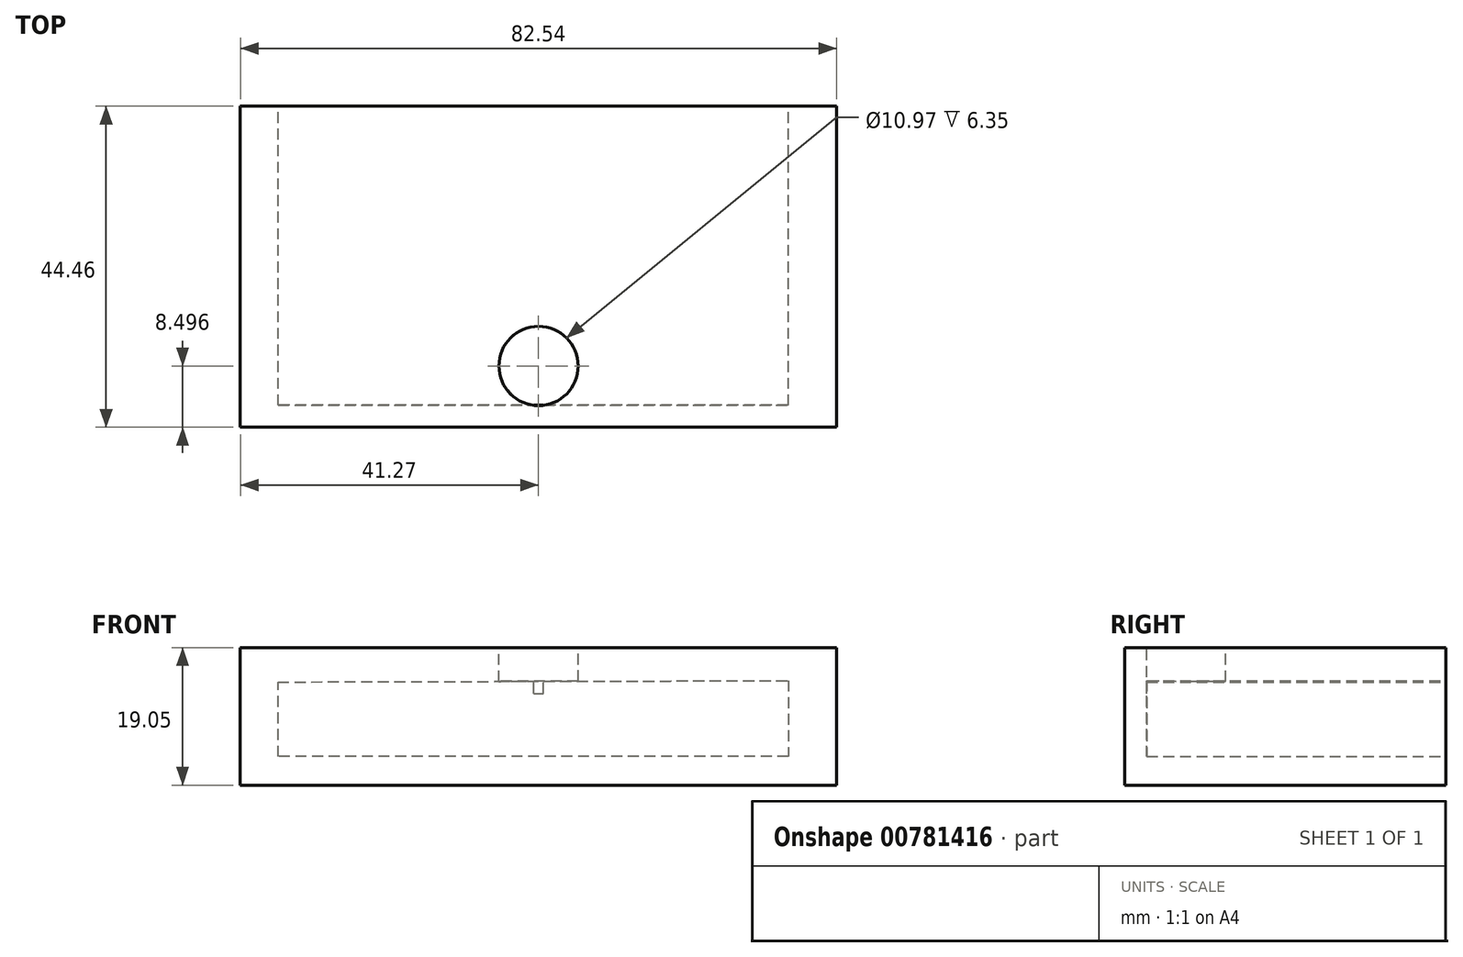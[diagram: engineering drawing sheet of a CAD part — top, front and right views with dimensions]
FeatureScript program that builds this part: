
annotation { "Feature Type Name" : "Feature", "Feature Type Description" : "" }
export const myFeature = defineFeature(function(context is Context, id is Id, definition is map)
    precondition{}
    {
        {
            var Q0;
            Q0=qCreatedBy(makeId("Top.planeOp"),FACE);
            var sketch = newSketch(context, id + "F0", { "sketchPlane" : qUnion([Q0])});
            skLineSegment(sketch, "E0.bottom", {"start": v(41.28, -22.22) * mm, "end": v(-41.28, -22.23) * mm});
            skLineSegment(sketch, "E0.top", {"start": v(41.28, 22.23) * mm, "end": v(-41.28, 22.23) * mm});
            skLineSegment(sketch, "E0.left", {"start": v(41.28, -22.22) * mm, "end": v(41.28, 22.23) * mm});
            skLineSegment(sketch, "E0.right", {"start": v(-41.28, -22.23) * mm, "end": v(-41.28, 22.23) * mm});
            skPoint(sketch, "E0.middle", {"position": v(0, 0) * mm});
            skSolve(sketch);
        }
        {
            var Q0;
            Q0 = qSketchRegion(id + "F0", true);
            extrude(context, id + "F1", {"entities" : qUnion([Q0]), "depth" : 19.05 * mm, "offsetDistance" : 25.4 * mm});
        }
        {
            var Q0;
            Q0=makeQuery(id+"F1.opExtrude","SWEPT_FACE",FACE,{"disambiguationData":[OSD([sQuery(id+"F0.wireOp",EDGE,"E0.top")])]});
            var sketch = newSketch(context, id + "F2", { "sketchPlane" : qUnion([Q0])});
            skLineSegment(sketch, "E1", {"start": v(-34.57, 14.47) * mm, "end": v(-34.57, 3.96) * mm});
            skLineSegment(sketch, "E2", {"start": v(-34.57, 3.96) * mm, "end": v(36.04, 3.96) * mm});
            skLineSegment(sketch, "E3", {"start": v(36.04, 3.96) * mm, "end": v(36.04, 14.29) * mm});
            skLineSegment(sketch, "E4", {"start": v(36.04, 14.29) * mm, "end": v(-34.57, 14.47) * mm});
            skSolve(sketch);
        }
        {
            var Q0;
            Q0 = qSketchRegion(id + "F2", true);
            extrude(context, id + "F3", {"entities" : qUnion([Q0]), "operationType" : NewBodyOperationType.REMOVE, "oppositeDirection" : true, "depth" : 41.4 * mm, "offsetDistance" : 25.4 * mm});
        }
        {
            var Q0;
            Q0=makeQuery(id+"F1.opExtrude","CAP_FACE",FACE,{"disambiguationData":[OSD([sQuery(id+"F0.wireOp",EDGE,"E0.bottom"),sQuery(id+"F0.wireOp",EDGE,"E0.top"),sQuery(id+"F0.wireOp",EDGE,"E0.left"),sQuery(id+"F0.wireOp",EDGE,"E0.right")])],"isStart":false});
            var sketch = newSketch(context, id + "F4", { "sketchPlane" : qUnion([Q0])});
            skCircle(sketch, "E5", {"center": v(0, -13.73) * mm, "radius": 5.49 * mm});
            skSolve(sketch);
        }
        {
            var Q0;
            Q0 = qSketchRegion(id + "F4", true);
            extrude(context, id + "F5", {"entities" : qUnion([Q0]), "operationType" : NewBodyOperationType.REMOVE, "oppositeDirection" : true, "depth" : 6.35 * mm, "offsetDistance" : 25.4 * mm});
        }
    });
